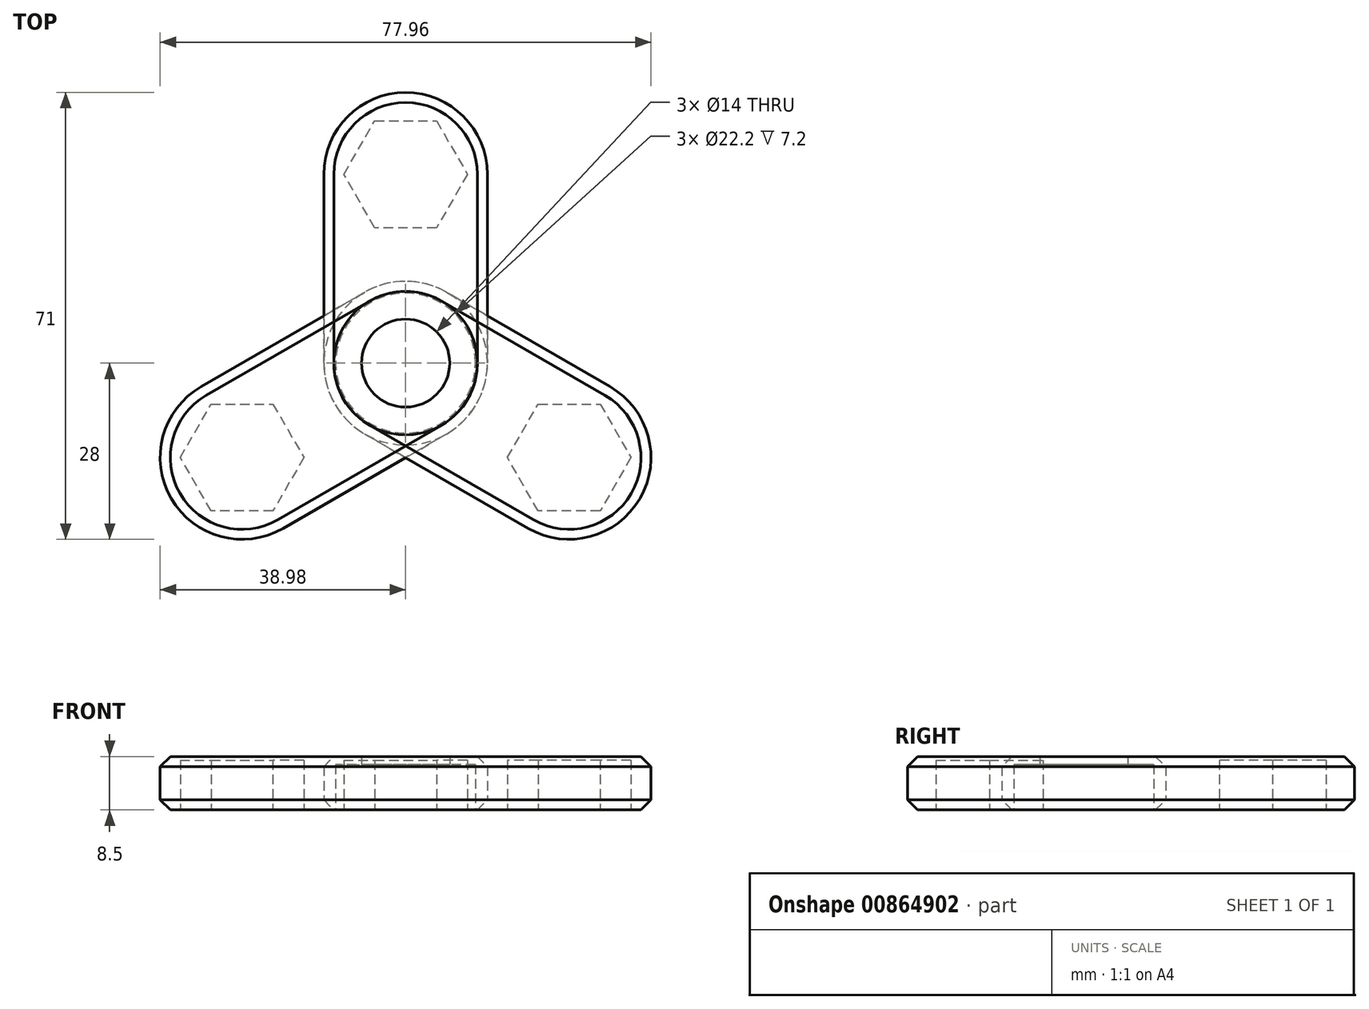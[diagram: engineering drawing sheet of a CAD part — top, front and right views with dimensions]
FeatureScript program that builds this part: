
annotation { "Feature Type Name" : "Feature", "Feature Type Description" : "" }
export const myFeature = defineFeature(function(context is Context, id is Id, definition is map)
    precondition{}
    {
        {
            var Q0;
            Q0=qCreatedBy(makeId("Top.planeOp"),FACE);
            var sketch = newSketch(context, id + "F0", { "sketchPlane" : qUnion([Q0])});
            skCircle(sketch, "E0", {"center": v(0, 0) * mm, "radius": 13 * mm});
            skCircle(sketch, "E1", {"center": v(0, 0) * mm, "radius": 11.1 * mm});
            skCircle(sketch, "E2", {"center": v(0, 30) * mm, "radius": 13 * mm});
            skCircle(sketch, "E3.cCircle", {"center": v(0, 30) * mm, "radius": 8.5 * mm, "construction": true});
            skLineSegment(sketch, "E3.0", {"start": v(9.81, 30) * mm, "end": v(4.9, 21.5) * mm});
            skLineSegment(sketch, "E3.1", {"start": v(4.9, 21.5) * mm, "end": v(-4.9, 21.5) * mm});
            skLineSegment(sketch, "E3.2", {"start": v(-4.9, 21.5) * mm, "end": v(-9.81, 30) * mm});
            skLineSegment(sketch, "E3.3", {"start": v(-9.81, 30) * mm, "end": v(-4.9, 38.5) * mm});
            skLineSegment(sketch, "E3.4", {"start": v(-4.9, 38.5) * mm, "end": v(4.9, 38.5) * mm});
            skLineSegment(sketch, "E3.5", {"start": v(4.9, 38.5) * mm, "end": v(9.81, 30) * mm});
            skPoint(sketch, "E3.0.midPoint", {"position": v(7.36, 25.75) * mm});
            skCircle(sketch, "E4", {"center": v(0, 0) * mm, "radius": 7 * mm});
            skLineSegment(sketch, "E5", {"start": v(-13, 0) * mm, "end": v(-13, 30) * mm});
            skLineSegment(sketch, "E6", {"start": v(13, 0) * mm, "end": v(13, 30) * mm});
            skSolve(sketch);
        }
        {
            var Q0;
            {var subQ0=sQuery(id+"F0.wireOp",EDGE,"E5");Q0=makeQuery(id+"F0.imprint","IMPRINT",FACE,{"disambiguationData":[TD([[makeQuery(id+"F0.imprint","IMPRINT",EDGE,{"derivedFrom":subQ0}),-1.0]])]});}
            var Q1;
            Q1=makeQuery(id+"F0.imprint","IMPRINT",FACE,{"disambiguationData":[TD([[makeQuery(id+"F0.imprint","IMPRINT",EDGE,{"derivedFrom":sQuery(id+"F0.wireOp",EDGE,"E3.0")}),1.0]])]});
            var Q2;
            Q2=makeQuery(id+"F0.imprint","IMPRINT",FACE,{"disambiguationData":[TD([[makeQuery(id+"F0.imprint","IMPRINT",EDGE,{"derivedFrom":sQuery(id+"F0.wireOp",EDGE,"E3.0")}),-1.0]])]});
            var Q3;
            Q3=makeQuery(id+"F0.imprint","IMPRINT",FACE,{"disambiguationData":[TD([[makeQuery(id+"F0.imprint","IMPRINT",EDGE,{"derivedFrom":sQuery(id+"F0.wireOp",EDGE,"E1")}),-1.0]])]});
            var Q4;
            Q4=makeQuery(id+"F0.imprint","IMPRINT",FACE,{"disambiguationData":[TD([[makeQuery(id+"F0.imprint","IMPRINT",EDGE,{"derivedFrom":sQuery(id+"F0.wireOp",EDGE,"E1")}),1.0]])]});
            extrude(context, id + "F1", {"entities" : qUnion([Q0, Q1, Q2, Q3, Q4]), "depth" : 8.5 * mm, "offsetDistance" : 25 * mm});
        }
        {
            var Q0;
            Q0=makeQuery(id+"F0.imprint","IMPRINT",FACE,{"disambiguationData":[TD([[makeQuery(id+"F0.imprint","IMPRINT",EDGE,{"derivedFrom":sQuery(id+"F0.wireOp",EDGE,"E3.0")}),-1.0]])]});
            extrude(context, id + "F2", {"entities" : qUnion([Q0]), "operationType" : NewBodyOperationType.REMOVE, "depth" : 7.9 * mm, "offsetDistance" : 25 * mm});
        }
        {
            var Q0;
            Q0=makeQuery(id+"F0.imprint","IMPRINT",FACE,{"disambiguationData":[TD([[makeQuery(id+"F0.imprint","IMPRINT",EDGE,{"derivedFrom":sQuery(id+"F0.wireOp",EDGE,"E1")}),1.0]])]});
            extrude(context, id + "F3", {"entities" : qUnion([Q0]), "operationType" : NewBodyOperationType.REMOVE, "depth" : 7.2 * mm, "offsetDistance" : 25 * mm});
        }
        {
            var Q0;
            Q0=makeQuery(id+"F1.opExtrude","SWEPT_BODY",BODY,{"disambiguationData":[OSD([sQuery(id+"F0.wireOp",EDGE,"E0"),sQuery(id+"F0.wireOp",EDGE,"E2"),sQuery(id+"F0.wireOp",EDGE,"E4"),sQuery(id+"F0.wireOp",EDGE,"E5"),sQuery(id+"F0.wireOp",EDGE,"E6")])]});
            var Q1;
            Q1=makeQuery(id+"F3.boolean.opBoolean","COPY",FACE,{"derivedFrom":makeQuery(id+"F3.opExtrude","SWEPT_FACE",FACE,{"disambiguationData":[OSD([sQuery(id+"F0.wireOp",EDGE,"E1")])]})});
            circularPattern(context, id + "F4", {"entities" : qUnion([Q0]), "axis" : qUnion([Q1]), "angle" : 360 * degree, "instanceCount" : 3, "equalSpace" : true});
        }
        {
            var Q0;
            Q0=makeQuery(id+"F4.opPattern","COPY",EDGE,{"derivedFrom":makeQuery(id+"F1.opExtrude","CAP_EDGE",EDGE,{"disambiguationData":[OSD([sQuery(id+"F0.wireOp",EDGE,"E5")])],"isStart":true}),"instanceName":"2"});
            var Q1;
            Q1=makeQuery(id+"F4.opPattern","COPY",EDGE,{"derivedFrom":makeQuery(id+"F1.opExtrude","CAP_EDGE",EDGE,{"disambiguationData":[OSD([sQuery(id+"F0.wireOp",EDGE,"E2")])],"isStart":true}),"instanceName":"2"});
            var Q2;
            Q2=makeQuery(id+"F4.opPattern","COPY",EDGE,{"derivedFrom":makeQuery(id+"F1.opExtrude","CAP_EDGE",EDGE,{"disambiguationData":[OSD([sQuery(id+"F0.wireOp",EDGE,"E6")])],"isStart":true}),"instanceName":"2"});
            var Q3;
            Q3=makeQuery(id+"F4.opPattern","COPY",EDGE,{"derivedFrom":makeQuery(id+"F1.opExtrude","CAP_EDGE",EDGE,{"disambiguationData":[OSD([sQuery(id+"F0.wireOp",EDGE,"E5")])],"isStart":true}),"instanceName":"1"});
            var Q4;
            Q4=makeQuery(id+"F4.opPattern","COPY",EDGE,{"derivedFrom":makeQuery(id+"F1.opExtrude","CAP_EDGE",EDGE,{"disambiguationData":[OSD([sQuery(id+"F0.wireOp",EDGE,"E2")])],"isStart":true}),"instanceName":"1"});
            var Q5;
            Q5=makeQuery(id+"F4.opPattern","COPY",EDGE,{"derivedFrom":makeQuery(id+"F1.opExtrude","CAP_EDGE",EDGE,{"disambiguationData":[OSD([sQuery(id+"F0.wireOp",EDGE,"E6")])],"isStart":true}),"instanceName":"1"});
            var Q6;
            Q6=makeQuery(id+"F1.opExtrude","CAP_EDGE",EDGE,{"disambiguationData":[OSD([sQuery(id+"F0.wireOp",EDGE,"E5")])],"isStart":true});
            var Q7;
            Q7=makeQuery(id+"F1.opExtrude","CAP_EDGE",EDGE,{"disambiguationData":[OSD([sQuery(id+"F0.wireOp",EDGE,"E6")])],"isStart":true});
            var Q8;
            Q8=makeQuery(id+"F1.opExtrude","CAP_EDGE",EDGE,{"disambiguationData":[OSD([sQuery(id+"F0.wireOp",EDGE,"E2")])],"isStart":true});
            var Q9;
            Q9=makeQuery(id+"F1.opExtrude","CAP_EDGE",EDGE,{"disambiguationData":[OSD([sQuery(id+"F0.wireOp",EDGE,"E6")])],"isStart":false});
            var Q10;
            Q10=makeQuery(id+"F4.opPattern","COPY",EDGE,{"derivedFrom":makeQuery(id+"F1.opExtrude","CAP_EDGE",EDGE,{"disambiguationData":[OSD([sQuery(id+"F0.wireOp",EDGE,"E5")])],"isStart":false}),"instanceName":"2"});
            var Q11;
            Q11=makeQuery(id+"F4.opPattern","COPY",EDGE,{"derivedFrom":makeQuery(id+"F1.opExtrude","CAP_EDGE",EDGE,{"disambiguationData":[OSD([sQuery(id+"F0.wireOp",EDGE,"E5")])],"isStart":false}),"instanceName":"1"});
            chamfer(context, id + "F5", {"entities" : qUnion([Q0, Q1, Q2, Q3, Q4, Q5, Q6, Q7, Q8, Q9, Q10, Q11]), "width" : 1.6 * mm, "tangentPropagation" : true});
        }
    });
